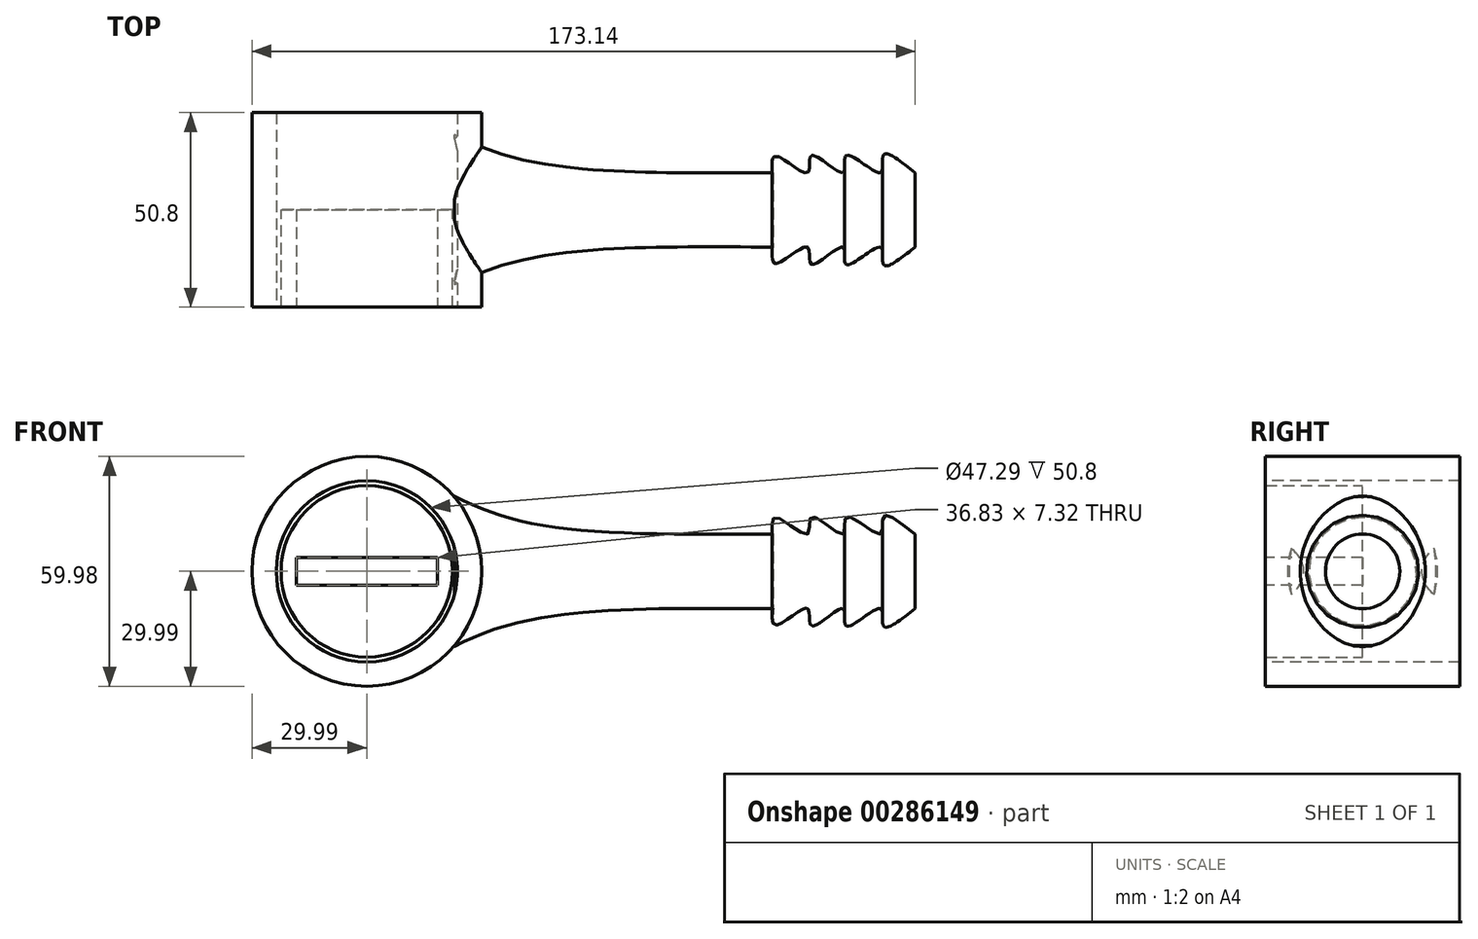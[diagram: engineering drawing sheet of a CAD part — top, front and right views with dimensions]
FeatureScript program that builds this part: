
annotation { "Feature Type Name" : "Feature", "Feature Type Description" : "" }
export const myFeature = defineFeature(function(context is Context, id is Id, definition is map)
    precondition{}
    {
        {
            var Q0;
            Q0=qCreatedBy(makeId("Front.planeOp"),FACE);
            var sketch = newSketch(context, id + "F0", { "sketchPlane" : qUnion([Q0])});
            skCircle(sketch, "E0", {"center": v(0, 0) * mm, "radius": 22.37 * mm});
            skSolve(sketch);
        }
        {
            var Q0;
            Q0 = qSketchRegion(id + "F0", true);
            extrude(context, id + "F1", {"entities" : qUnion([Q0]), "depth" : 25.4 * mm});
        }
        {
            var Q0;
            Q0=makeQuery(id+"F1.opExtrude","CAP_FACE",FACE,{"disambiguationData":[OSD([sQuery(id+"F0.wireOp",EDGE,"E0")])],"isStart":false});
            var sketch = newSketch(context, id + "F2", { "sketchPlane" : qUnion([Q0])});
            skLineSegment(sketch, "E1.bottom", {"start": v(-18.41, 3.66) * mm, "end": v(18.41, 3.66) * mm});
            skLineSegment(sketch, "E1.top", {"start": v(-18.41, -3.66) * mm, "end": v(18.41, -3.66) * mm});
            skLineSegment(sketch, "E1.left", {"start": v(-18.41, 3.66) * mm, "end": v(-18.41, -3.66) * mm});
            skLineSegment(sketch, "E1.right", {"start": v(18.41, 3.66) * mm, "end": v(18.41, -3.66) * mm});
            skSolve(sketch);
        }
        {
            var Q0;
            Q0=makeQuery(id+"F2.imprint","IMPRINT",FACE,{"disambiguationData":[TD([[makeQuery(id+"F2.imprint","IMPRINT",EDGE,{"derivedFrom":sQuery(id+"F2.wireOp",EDGE,"E1.bottom")}),-1.0]])]});
            extrude(context, id + "F3", {"entities" : qUnion([Q0]), "operationType" : NewBodyOperationType.REMOVE, "oppositeDirection" : true, "depth" : 25.4 * mm});
        }
        {
            var Q0;
            Q0=makeQuery(id+"F1.opExtrude","CAP_FACE",FACE,{"disambiguationData":[OSD([sQuery(id+"F0.wireOp",EDGE,"E0")])],"isStart":false});
            var sketch = newSketch(context, id + "F4", { "sketchPlane" : qUnion([Q0])});
            skCircle(sketch, "E2.0", {"center": v(0, 0) * mm, "radius": 23.64 * mm});
            skCircle(sketch, "E3.0", {"center": v(0, 0) * mm, "radius": 30 * mm});
            skSolve(sketch);
        }
        {
            var Q0;
            Q0 = qSketchRegion(id + "F4", true);
            extrude(context, id + "F5", {"entities" : qUnion([Q0]), "oppositeDirection" : true, "depth" : 50.8 * mm});
        }
        {
            var Q0;
            Q0=qCreatedBy(makeId("Front.planeOp"),FACE);
            var sketch = newSketch(context, id + "F6", { "sketchPlane" : qUnion([Q0])});
            skLineSegment(sketch, "E4", {"start": v(-62.97, 0) * mm, "end": v(117.43, 0) * mm});
            skSolve(sketch);
        }
        {
            var Q0;
            Q0=qCreatedBy(makeId("Front.planeOp"),FACE);
            var sketch = newSketch(context, id + "F7", { "sketchPlane" : qUnion([Q0])});
            skFitSpline(sketch, "E5", {"points": [v(22.86, 19.59) * mm, v(45.72, 12.05) * mm, v(106.04, 9.73) * mm], "startDerivative": vector(52.54, -26.9) * mm, "endDerivative": vector(129.76, 0.97) * mm});
            skLineSegment(sketch, "E6", {"start": v(26.62, 0) * mm, "end": v(143.15, 0) * mm});
            skLineSegment(sketch, "E7", {"start": v(143.15, 0) * mm, "end": v(143.15, 9.73) * mm});
            skFitSpline(sketch, "E8", {"points": [v(143.15, 9.73) * mm, v(134.9, 14.27) * mm, v(134.08, 9.73) * mm, v(125.21, 14.27) * mm, v(124.39, 9.73) * mm, v(116.14, 14.27) * mm, v(115.1, 9.73) * mm, v(106.86, 14.06) * mm, v(106.04, 9.73) * mm], "startDerivative": vector(-76.73, 60.13) * mm, "endDerivative": vector(6.58, -63.21) * mm});
            skLineSegment(sketch, "E9", {"start": v(22.86, 19.59) * mm, "end": v(26.62, 0) * mm});
            skSolve(sketch);
        }
        {
            var Q0;
            Q0 = qSketchRegion(id + "F7", true);
            var Q1;
            Q1=sQuery(id+"F7.wireOp",EDGE,"E6");
            revolve(context, id + "F8", {"operationType" : NewBodyOperationType.ADD, "entities" : qUnion([Q0]), "axis" : qUnion([Q1]), "revolveType" : RevolveType.FULL});
        }
    });
